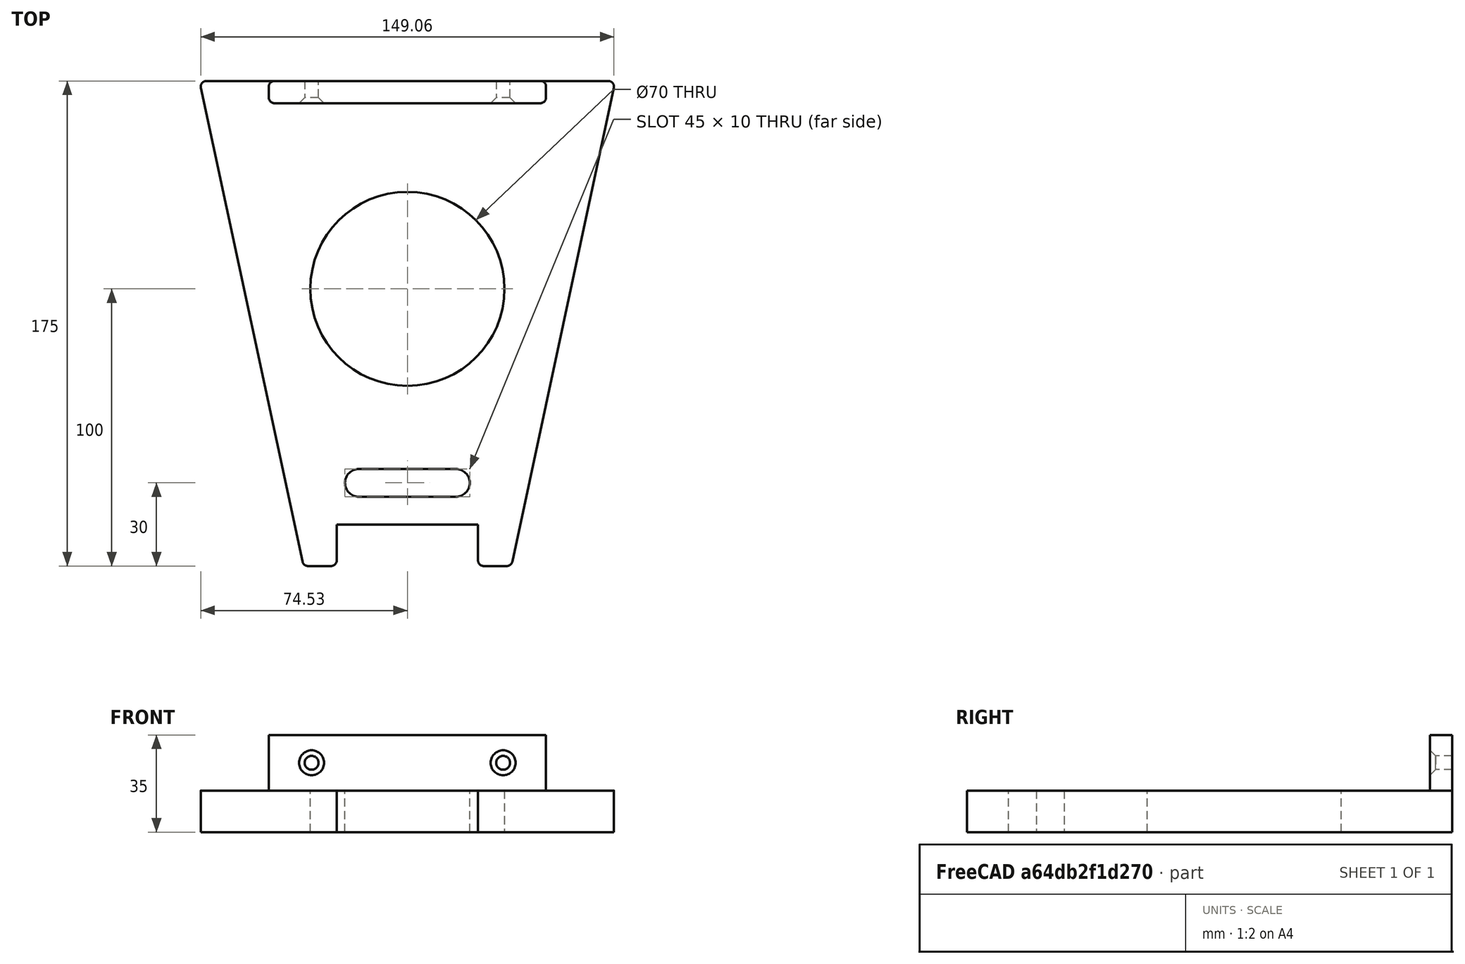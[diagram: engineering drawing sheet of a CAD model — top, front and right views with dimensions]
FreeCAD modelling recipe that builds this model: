
FCSTD DOCUMENT  (FreeCAD 0.19R)
Label: LackBrace
License: All rights reserved
LicenseURL: http://en.wikipedia.org/wiki/All_rights_reserved
objects: Sketcher::SketchObject×5, PartDesign::Pocket×3, PartDesign::Pad×2, PartDesign::Fillet×2, PartDesign::Chamfer×1, PartDesign::Body×1, Mesh::Feature×1
note: 22 computed .brp shape members not serialized (recipe doc carries the construction recipe); baked Part::Feature solids carry a one-line shape summary decoded from their .brp

FEATURE [Sketcher::SketchObject] Sketch
  FullyConstrained = true
  MapMode = 5
  Support = -> [XY_Plane]
  sketch-geometry (8):
    g0: LineSegment StartX=-75 StartY=0 StartZ=0 EndX=75 EndY=0 EndZ=0
    g1: LineSegment StartX=75 StartY=0 StartZ=0 EndX=37.5 EndY=-175 EndZ=0
    g2: LineSegment StartX=37.5 StartY=-175 StartZ=0 EndX=25.5 EndY=-175 EndZ=0
    g3: LineSegment StartX=25.5 StartY=-175 StartZ=0 EndX=25.5 EndY=-160 EndZ=0
    g4: LineSegment StartX=25.5 StartY=-160 StartZ=0 EndX=-25.5 EndY=-160 EndZ=0
    g5: LineSegment StartX=-25.5 StartY=-160 StartZ=0 EndX=-25.5 EndY=-175 EndZ=0
    g6: LineSegment StartX=-25.5 StartY=-175 StartZ=0 EndX=-37.5 EndY=-175 EndZ=0
    g7: LineSegment StartX=-37.5 StartY=-175 StartZ=0 EndX=-75 EndY=0 EndZ=0
  constraints (21):
    c: Coincident(g0,g1)
    c: Coincident(g1,g2)
    c: Horizontal(g2)
    c: Coincident(g2,g3)
    c: Vertical(g3)
    c: Coincident(g3,g4)
    c: Coincident(g4,g5)
    c: Coincident(g5,g6)
    c: Coincident(g6,g7)
    c: Coincident(g7,g0)
    c: Symmetric(g0,g0,g-2)
    c: Symmetric(g3,g4,g-2)
    c: Symmetric(g6,g1,g-2)
    c: Horizontal(g6)
    c: Equal(g2,g6)
    c: Distance(g3,g0) = 160
    c: Distance(g0) = 150
    c: Distance(g3) = 15
    c: Distance(g4) = 51
    c: Distance(g2) = 12
    c: PointOnObject(g0,g-1)
FEATURE [PartDesign::Pad] Pad
  Direction = (1,1,1)
  Length = 15
  Length2 = 100
  Profile = -> Sketch
  Type = 0
FEATURE [Sketcher::SketchObject] Sketch001
  FullyConstrained = true
  MapMode = 5
  Placement = pos=(0,0,15) rot=(0,0,1;0rad)
  Support = -> [Pad]
  sketch-geometry (4):
    g0: LineSegment StartX=-50 StartY=0 StartZ=0 EndX=50 EndY=0 EndZ=0
    g1: LineSegment StartX=50 StartY=0 StartZ=0 EndX=50 EndY=-8 EndZ=0
    g2: LineSegment StartX=50 StartY=-8 StartZ=0 EndX=-50 EndY=-8 EndZ=0
    g3: LineSegment StartX=-50 StartY=-8 StartZ=0 EndX=-50 EndY=0 EndZ=0
  constraints (11):
    c: Coincident(g0,g1)
    c: Coincident(g1,g2)
    c: Coincident(g2,g3)
    c: Coincident(g3,g0)
    c: Horizontal(g0)
    c: Horizontal(g2)
    c: Vertical(g1)
    c: Vertical(g3)
    c: Distance(g1) = 8
    c: Symmetric(g0,g0,g-1)
    c: Distance(g2) = 100
FEATURE [PartDesign::Pad] Pad001
  BaseFeature = -> Pad
  Direction = (1,1,1)
  Length = 20
  Length2 = 100
  Profile = -> Sketch001
  Type = 0
FEATURE [Sketcher::SketchObject] Sketch002
  FullyConstrained = false
  MapMode = 5
  Placement = pos=(0,-8,0) rot=(1,0,0;1.5708rad)
  Support = -> [Pad001]
  sketch-geometry (2):
    g0: Circle CenterX=-34.5471 CenterY=25 CenterZ=0 NormalX=0 NormalY=0 NormalZ=1 AngleXU=0 Radius=2.5
    g1: Circle CenterX=34.5471 CenterY=25 CenterZ=0 NormalX=0 NormalY=0 NormalZ=1 AngleXU=0 Radius=2.5
  constraints (4):
    c: Diameter(g1) = 5
    c: Equal(g1,g0)
    c: Symmetric(g1,g0,g-2)
    c: DistanceY(g1) = 25
FEATURE [PartDesign::Pocket] Pocket
  BaseFeature = -> Pad001
  Length = 5
  Length2 = 100
  Profile = -> Sketch002
  Type = 1
FEATURE [PartDesign::Fillet] Fillet
  Base = -> Pocket [Edge10,Edge7,Edge31,Edge32,Edge2,Edge1]
  BaseFeature = -> Pocket
  Radius = 2
  SupportTransform = false
FEATURE [PartDesign::Fillet] Fillet001
  Base = -> Fillet [Edge38,Edge53,Edge55,Edge40]
  BaseFeature = -> Fillet
  Radius = 2
  SupportTransform = false
FEATURE [PartDesign::Chamfer] Chamfer
  Angle = 45
  Base = -> Fillet001 [Edge34,Edge35]
  BaseFeature = -> Fillet001
  ChamferType = 0
  FlipDirection = false
  Size = 2
  Size2 = 1
  SupportTransform = false
FEATURE [Sketcher::SketchObject] Sketch003
  FullyConstrained = true
  MapMode = 5
  Placement = pos=(0,0,15) rot=(0,0,1;0rad)
  Support = -> [Chamfer]
  sketch-geometry (1):
    g0: Circle CenterX=0 CenterY=-75 CenterZ=0 NormalX=0 NormalY=0 NormalZ=1 AngleXU=0 Radius=35
  constraints (3):
    c: PointOnObject(g0,g-2)
    c: Diameter(g0) = 70
    c: DistanceY(g0) = -75
FEATURE [PartDesign::Pocket] Pocket001
  BaseFeature = -> Chamfer
  Length = 5
  Length2 = 100
  Profile = -> Sketch003
  Type = 1
FEATURE [Sketcher::SketchObject] Sketch004
  FullyConstrained = true
  MapMode = 5
  Placement = pos=(0,0,15) rot=(0,0,1;0rad)
  Support = -> [Pocket001]
  sketch-geometry (4):
    g0: ArcOfCircle CenterX=-17.5 CenterY=-145 CenterZ=0 NormalX=0 NormalY=0 NormalZ=1 AngleXU=0 Radius=5 StartAngle=1.5708 EndAngle=4.71239
    g1: ArcOfCircle CenterX=17.5 CenterY=-145 CenterZ=0 NormalX=0 NormalY=0 NormalZ=1 AngleXU=0 Radius=5 StartAngle=4.71239 EndAngle=7.85398
    g2: LineSegment StartX=-17.5 StartY=-150 StartZ=0 EndX=17.5 EndY=-150 EndZ=0
    g3: LineSegment StartX=-17.5 StartY=-140 StartZ=0 EndX=17.5 EndY=-140 EndZ=0
  constraints (9):
    c: Tangent(g0,g3) = 1.5708
    c: Tangent(g0,g2) = -1.5708
    c: Tangent(g2,g1) = -1.5708
    c: Tangent(g3,g1) = 1.5708
    c: Horizontal(g2)
    c: Distance(g1,g1) = 10
    c: Symmetric(g1,g0,g-2)
    c: Distance(g3) = 35
    c: DistanceY(g1) = -145
FEATURE [PartDesign::Pocket] Pocket002
  BaseFeature = -> Pocket001
  Length = 5
  Length2 = 100
  Profile = -> Sketch004
  Type = 1
FEATURE [PartDesign::Body] Body
  Group = -> [Sketch,Pad,Sketch001,Pad001,Sketch002,Pocket,Fillet,Fillet001,Chamfer,Sketch003,Pocket001,Sketch004,Pocket002]
  Origin = -> Origin
  Tip = -> Pocket002
FEATURE [Mesh::Feature] Mesh  label="Pocket002 (Meshed)"
